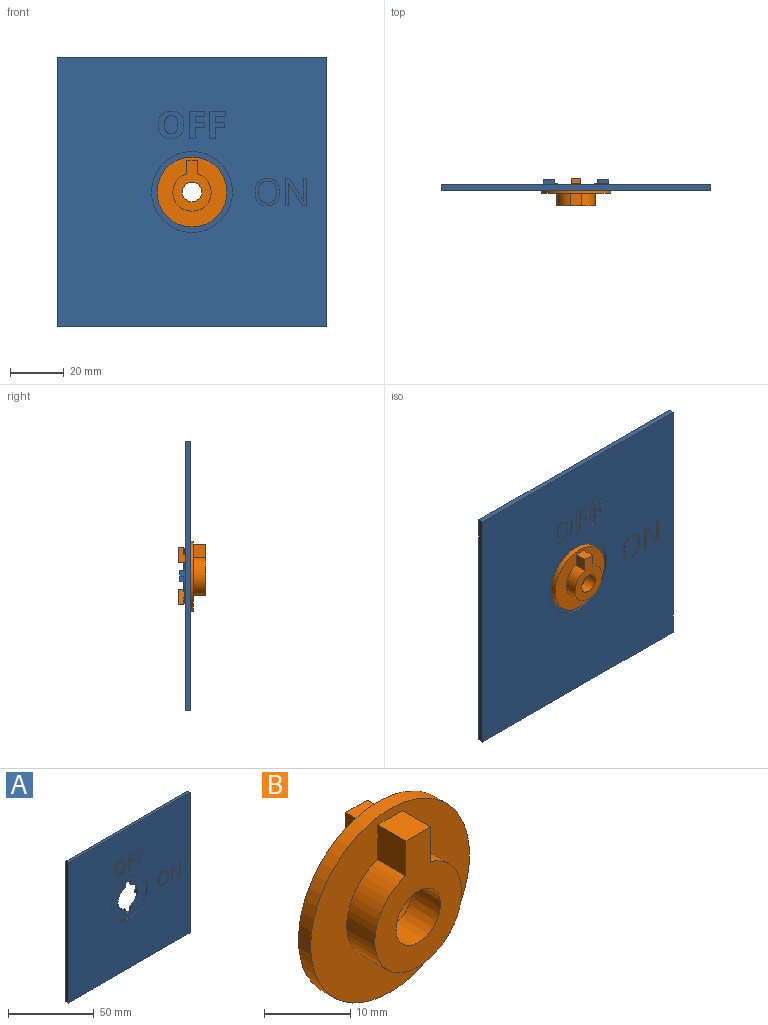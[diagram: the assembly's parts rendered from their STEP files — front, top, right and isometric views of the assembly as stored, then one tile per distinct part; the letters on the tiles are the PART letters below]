
ASSEMBLY  parts=2 mates=1
PART A: 110 faces, bbox 100.1x4.1x100.1 mm
  f0: plane 100x100mm, normal (0,-1,0), area 9039.8mm2, adj f10,f11,f12,f13,f23,f36,f37,f38
  f1: cylinder r=8.25mm len=16.01mm, axis (0,1,0), area 26.5mm2, adj f3,f6,f9,f14,f15,f17,f22,f27
  f2: cylinder r=8.25mm len=16.01mm, axis (0,1,0), area 26.5mm2, adj f4,f7,f9,f18,f19,f21,f22,f25
  f3: plane 3x1mm, normal (1,0,0), area 3mm2, adj f1,f5,f9,f22
  f4: plane 3x1mm, normal (-1,0,0), area 3mm2, adj f2,f5,f9,f22
  f5: plane 4x1mm, normal (0,0,-1), area 4mm2, adj f3,f4,f9,f22
  f6: plane 3x1mm, normal (1,0,0), area 3mm2, adj f1,f8,f9,f22
  f7: plane 3x1mm, normal (-1,0,0), area 3mm2, adj f2,f8,f9,f22
  f8: plane 4x1mm, normal (0,0,1), area 4mm2, adj f6,f7,f9,f22
  f9: plane 100.09x100.09mm, normal (0,1,0), area 9660mm2, adj f1,f2,f3,f4,f5,f6,f7,f8
  f10: plane 100x2mm, normal (0,0,1), area 200mm2, adj f0,f9,f11,f13
  f11: plane 100x2mm, normal (-1,0,0), area 200mm2, adj f0,f9,f10,f12
  f12: plane 100x2mm, normal (0,0,-1), area 200mm2, adj f0,f9,f11,f13
  f13: plane 100x2mm, normal (1,0,0), area 200mm2, adj f0,f9,f10,f12
  f14: plane 4x1.4mm, normal (0,0,-1), area 5.6mm2, adj f1,f16,f17,f27
  f15: plane 4.25x2mm, normal (0,0,1), area 8.5mm2, adj f1,f9,f16,f17
  f16: plane 2x2mm, normal (-1,0,0), area 4mm2, adj f9,f14,f15,f17,f26
  f17: plane 4.25x2mm, normal (0,1,0), area 8.2mm2, adj f1,f14,f15,f16
  f18: plane 4x1.4mm, normal (0,0,1), area 5.6mm2, adj f2,f20,f21,f25
  f19: plane 4.25x2mm, normal (0,0,-1), area 8.5mm2, adj f2,f9,f20,f21
  f20: plane 2x2mm, normal (1,0,0), area 4mm2, adj f9,f18,f19,f21,f24
  f21: plane 4.25x2mm, normal (0,1,0), area 8.2mm2, adj f2,f18,f19,f20
  f22: plane 30x30mm, normal (0,-1,0), area 470.4mm2, adj f1,f2,f3,f4,f5,f6,f7,f8
  f23: cylinder r=15mm len=30mm, axis (0,-1,0), area 94.2mm2, adj f0,f22
  f24: cylinder r=12.25mm len=4.19mm, axis (0,-1,0), area 2.6mm2, adj f9,f20,f25,f33
  f25: plane 4.51x4.2mm, normal (0,1,0), area 14.3mm2, adj f2,f18,f24,f32
  f26: cylinder r=12.25mm len=4.19mm, axis (0,-1,0), area 2.6mm2, adj f9,f16,f27,f28
  f27: plane 4.51x4.2mm, normal (0,1,0), area 14.3mm2, adj f1,f14,f26,f30
  f28: bspline ~6.77x6.06mm, area 2.7mm2, adj f9,f26,f30,f109
  f29: bspline ~8.11x7.84mm, area 0.1mm2, adj f1,f31,f109
  f30: bspline ~7.7x7.29mm, area 27.5mm2, adj f27,f28,f31,f109
  f31: bspline ~4.56x4.08mm, area 3.5mm2, adj f1,f29,f30,f109
  f32: bspline ~7.7x7.29mm, area 27.5mm2, adj f25,f33,f35,f108
  f33: bspline ~6.77x6.06mm, area 2.7mm2, adj f9,f24,f32,f108
  f34: bspline ~8.11x7.84mm, area 0.1mm2, adj f2,f35,f108
  f35: bspline ~4.56x4.08mm, area 3.5mm2, adj f2,f32,f34,f108
  f36: plane 2.07x0.5mm, normal (0,0,1), area 1mm2, adj f0,f37,f45,f46
  f37: plane 3.92x0.5mm, normal (-1,0,0), area 2mm2, adj f0,f36,f38,f46
  f38: plane 3.36x0.5mm, normal (0,0,1), area 1.7mm2, adj f0,f37,f39,f46
  f39: plane 1.72x0.5mm, normal (-1,0,0), area 0.9mm2, adj f0,f38,f40,f46
  f40: plane 3.36x0.5mm, normal (0,0,-1), area 1.7mm2, adj f0,f39,f41,f46
  f41: plane 2.56x0.5mm, normal (-1,0,0), area 1.3mm2, adj f0,f40,f42,f46
  f42: plane 3.62x0.5mm, normal (0,0,1), area 1.8mm2, adj f0,f41,f43,f46
  f43: plane 1.72x0.5mm, normal (-1,0,0), area 0.9mm2, adj f0,f42,f44,f46
  f44: plane 5.68x0.5mm, normal (0,0,-1), area 2.8mm2, adj f0,f43,f45,f46
  f45: plane 9.92x0.5mm, normal (1,0,0), area 5mm2, adj f0,f36,f44,f46
  f46: plane 9.92x5.68mm, normal (0,-1,0), area 32.5mm2, adj f36,f37,f38,f39,f40,f41,f42,f43
  f47: extruded ~3.06x0.86mm, area 1.6mm2, adj f48,f62,f63,f106
  f48: extruded ~3.03x0.86mm, area 1.6mm2, adj f47,f49,f63,f106
  f49: extruded ~2.51x1.04mm, area 1.4mm2, adj f48,f50,f63,f106
  f50: extruded ~2.48x1.03mm, area 1.4mm2, adj f49,f51,f63,f106
  f51: extruded ~3.04x0.84mm, area 1.6mm2, adj f50,f52,f63,f106
  f52: extruded ~3.06x0.84mm, area 1.6mm2, adj f51,f53,f63,f106
  f53: extruded ~2.49x1.04mm, area 1.4mm2, adj f52,f62,f63,f106
  f54: extruded ~3.74x1.2mm, area 2mm2, adj f0,f55,f61,f63
  f55: extruded ~3.74x1.2mm, area 2mm2, adj f0,f54,f56,f63
  f56: extruded ~3.34x1.36mm, area 1.9mm2, adj f0,f55,f57,f63
  f57: extruded ~3.39x1.33mm, area 1.9mm2, adj f0,f56,f58,f63
  f58: extruded ~3.75x1.19mm, area 2mm2, adj f0,f57,f59,f63
  f59: extruded ~3.78x1.19mm, area 2mm2, adj f0,f58,f60,f63
  f60: extruded ~3.38x1.34mm, area 1.9mm2, adj f0,f59,f61,f63
  f61: extruded ~3.35x1.36mm, area 1.9mm2, adj f0,f54,f60,f63
  f62: extruded ~2.49x1.04mm, area 1.4mm2, adj f47,f53,f63,f106
  f63: plane 10.21x9.12mm, normal (0,-1,0), area 31.1mm2, adj f47,f48,f49,f50,f51,f52,f53,f54
  f64: extruded ~2.5x0.63mm, area 1.3mm2, adj f65,f77,f78,f107
  f65: extruded ~2.5x0.64mm, area 1.3mm2, adj f64,f66,f78,f107
  f66: extruded ~1.89x0.84mm, area 1.1mm2, adj f65,f67,f78,f107
  f67: extruded ~3.35x2.5mm, area 2.4mm2, adj f66,f68,f78,f107
  f68: extruded ~3.34x2.52mm, area 2.4mm2, adj f67,f77,f78,f107
  f69: extruded ~3.79x1.22mm, area 2mm2, adj f0,f70,f76,f78
  f70: extruded ~3.78x1.21mm, area 2mm2, adj f0,f69,f71,f78
  f71: extruded ~3.5x1.32mm, area 1.9mm2, adj f0,f70,f72,f78
  f72: extruded ~3.51x1.31mm, area 1.9mm2, adj f0,f71,f73,f78
  f73: extruded ~3.78x1.22mm, area 2mm2, adj f0,f72,f74,f78
  f74: extruded ~3.8x1.22mm, area 2mm2, adj f0,f73,f75,f78
  f75: extruded ~3.5x1.32mm, area 1.9mm2, adj f0,f74,f76,f78
  f76: extruded ~3.5x1.32mm, area 1.9mm2, adj f0,f69,f75,f78
  f77: extruded ~1.88x0.84mm, area 1.1mm2, adj f64,f68,f78,f107
  f78: plane 10.21x9.44mm, normal (0,-1,0), area 51.5mm2, adj f64,f65,f66,f67,f68,f69,f70,f71
  f79: plane 1.32x0.5mm, normal (0,0,1), area 0.7mm2, adj f0,f80,f93,f94
  f80: plane 9.92x0.5mm, normal (-1,0,0), area 5mm2, adj f0,f79,f81,f94
  f81: plane 1.08x0.5mm, normal (0,0,-1), area 0.5mm2, adj f0,f80,f82,f94
  f82: plane 5.69x0.5mm, normal (1,0,0), area 2.8mm2, adj f0,f81,f83,f94
  f83: extruded ~1.42x0.5mm, area 0.7mm2, adj f0,f82,f84,f94
  f84: extruded ~1.18x0.5mm, area 0.6mm2, adj f0,f83,f85,f94
  f85: plane 0.5x0.05mm, normal (0,0,-1), area 0mm2, adj f0,f84,f86,f94
  f86: plane 8.29x5.41mm, normal (-0.84,0,-0.55), area 4.9mm2, adj f0,f85,f87,f94
  f87: plane 1.3x0.5mm, normal (0,0,-1), area 0.7mm2, adj f0,f86,f88,f94
  f88: plane 9.92x0.5mm, normal (1,0,0), area 5mm2, adj f0,f87,f89,f94
  f89: plane 1.07x0.5mm, normal (0,0,1), area 0.5mm2, adj f0,f88,f90,f94
  f90: plane 5.64x0.5mm, normal (-1,0,0), area 2.8mm2, adj f0,f89,f91,f94
  f91: extruded ~2.68x0.5mm, area 1.3mm2, adj f0,f90,f92,f94
  f92: plane 0.5x0.05mm, normal (0,0,1), area 0mm2, adj f0,f91,f93,f94
  f93: plane 8.32x5.42mm, normal (0.84,0,0.55), area 5mm2, adj f0,f79,f92,f94
  f94: plane 9.92x7.75mm, normal (0,-1,0), area 32.5mm2, adj f79,f80,f81,f82,f83,f84,f85,f86
  f95: plane 2.07x0.5mm, normal (0,0,1), area 1mm2, adj f0,f96,f104,f105
  f96: plane 3.92x0.5mm, normal (-1,0,0), area 2mm2, adj f0,f95,f97,f105
  f97: plane 3.36x0.5mm, normal (0,0,1), area 1.7mm2, adj f0,f96,f98,f105
  f98: plane 1.72x0.5mm, normal (-1,0,0), area 0.9mm2, adj f0,f97,f99,f105
  f99: plane 3.36x0.5mm, normal (0,0,-1), area 1.7mm2, adj f0,f98,f100,f105
  f100: plane 2.56x0.5mm, normal (-1,0,0), area 1.3mm2, adj f0,f99,f101,f105
  f101: plane 3.62x0.5mm, normal (0,0,1), area 1.8mm2, adj f0,f100,f102,f105
  f102: plane 1.72x0.5mm, normal (-1,0,0), area 0.9mm2, adj f0,f101,f103,f105
  f103: plane 5.68x0.5mm, normal (0,0,-1), area 2.8mm2, adj f0,f102,f104,f105
  f104: plane 9.92x0.5mm, normal (1,0,0), area 5mm2, adj f0,f95,f103,f105
  f105: plane 9.92x5.68mm, normal (0,-1,0), area 32.5mm2, adj f95,f96,f97,f98,f99,f100,f101,f102
  f106: plane 8.17x6.68mm, normal (0,-1,0), area 45.2mm2, adj f47,f48,f49,f50,f51,f52,f53,f62
  f107: plane 6.69x5.03mm, normal (0,-1,0), area 28mm2, adj f64,f65,f66,f67,f68,f77
  f108: bspline ~5.46x3.36mm, area 2mm2, adj f2,f9,f32,f33,f34,f35
  f109: bspline ~5.46x3.36mm, area 2mm2, adj f1,f9,f28,f29,f30,f31
PART B: 24 faces, bbox 26x10.1x26 mm
  f0: plane 5.6x3.5mm, normal (0,1,0), area 17mm2, adj f10,f12,f13,f23
  f1: plane 3.5x2.58mm, normal (0,0,1), area 9mm2, adj f2,f6,f9,f22
  f2: plane 5.6x3.5mm, normal (0,1,0), area 17mm2, adj f1,f9,f15,f22
  f3: cylinder r=8.2mm len=3.08mm, axis (0,-1,0), area 4.7mm2, adj f4,f6,f9,f22
  f4: plane 3.5x2.6mm, normal (0,-1,0), area 8.1mm2, adj f3,f9,f15,f22
  f5: plane 26x26mm, normal (0,-1,0), area 353.6mm2, adj f7,f16,f19,f20,f21
  f6: plane 26x26mm, normal (0,1,0), area 467.8mm2, adj f1,f3,f7,f8,f9,f10,f11,f12
  f7: cylinder r=13mm len=26mm, axis (0,1,0), area 163.4mm2, adj f5,f6
  f8: cylinder r=3.8mm len=7.6mm, axis (0,1,0), area 47.8mm2, adj f6,f18
  f9: plane 5.6x3.5mm, normal (1,0,0), area 15.7mm2, adj f1,f2,f3,f4,f6,f15
  f10: plane 5.6x3.5mm, normal (-1,0,0), area 15.7mm2, adj f0,f6,f11,f12,f13,f14
  f11: cylinder r=8.2mm len=3.08mm, axis (0,-1,0), area 4.7mm2, adj f6,f10,f14,f23
  f12: plane 3.5x2.58mm, normal (0,0,-1), area 9mm2, adj f0,f6,f10,f23
  f13: plane 3.5x2mm, normal (0,0,1), area 7mm2, adj f0,f10,f14,f23
  f14: plane 3.5x2.6mm, normal (0,-1,0), area 8.1mm2, adj f10,f11,f13,f23
  f15: plane 3.5x2mm, normal (0,0,-1), area 7mm2, adj f2,f4,f9,f22
  f16: cylinder r=7.1mm len=14.2mm, axis (0,-1,0), area 186.6mm2, adj f5,f17,f19,f20
  f17: plane 18.85x14.2mm, normal (0,-1,0), area 135.7mm2, adj f16,f18,f19,f20,f21
  f18: cone r=3.64mm half-angle=2deg, axis (0,1,0), area 107.6mm2, adj f8,f17
  f19: plane 4.94x4.6mm, normal (1,0,0), area 22.7mm2, adj f5,f16,f17,f21
  f20: plane 4.94x4.6mm, normal (-1,0,0), area 22.7mm2, adj f5,f16,f17,f21
  f21: plane 4.6x4mm, normal (0,0,1), area 18.4mm2, adj f5,f17,f19,f20
  f22: plane 5.6x3.5mm, normal (-0.99,0,0.16), area 16mm2, adj f1,f2,f3,f4,f6,f15
  f23: plane 5.6x3.5mm, normal (0.99,0,-0.16), area 16mm2, adj f0,f6,f11,f12,f13,f14
PLACE A at identity fixed
PLACE B rot(axis=(0,1,0),0deg) t=(0,0,0)mm
MATE revolute B.f8 <-> A.f1  axis (0,1,0) through (0,-1,0)mm
